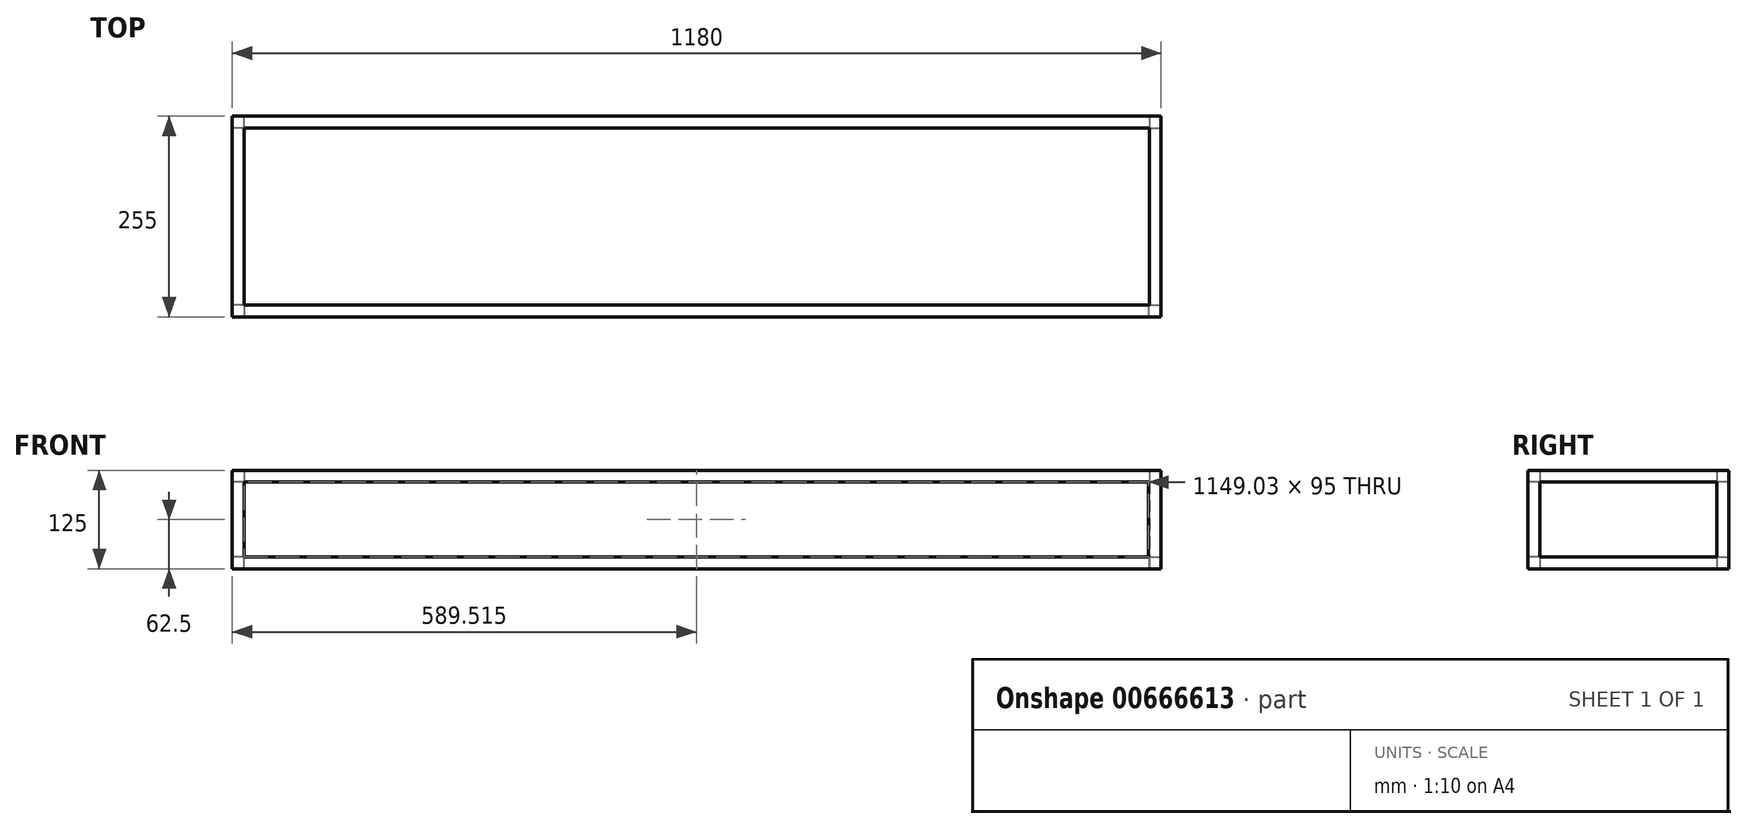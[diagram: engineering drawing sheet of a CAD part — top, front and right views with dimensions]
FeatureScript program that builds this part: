
annotation { "Feature Type Name" : "Feature", "Feature Type Description" : "" }
export const myFeature = defineFeature(function(context is Context, id is Id, definition is map)
    precondition{}
    {
        {
            var Q0;
            Q0=qCreatedBy(makeId("Top.planeOp"),FACE);
            var sketch = newSketch(context, id + "F0", { "sketchPlane" : qUnion([Q0])});
            skLineSegment(sketch, "E0.bottom", {"start": v(0, 0) * mm, "end": v(-1180, 0) * mm});
            skLineSegment(sketch, "E0.top", {"start": v(0, 255) * mm, "end": v(-1180, 255) * mm});
            skLineSegment(sketch, "E0.left", {"start": v(0, 0) * mm, "end": v(0, 255) * mm});
            skLineSegment(sketch, "E0.right", {"start": v(-1180, 0) * mm, "end": v(-1180, 255) * mm});
            skLineSegment(sketch, "E1.0", {"start": v(-15, 240) * mm, "end": v(-1165, 240) * mm});
            skLineSegment(sketch, "E1.1", {"start": v(-15, 15) * mm, "end": v(-15, 240) * mm});
            skLineSegment(sketch, "E1.2", {"start": v(-15, 15) * mm, "end": v(-1165, 15) * mm});
            skLineSegment(sketch, "E1.3", {"start": v(-1165, 15) * mm, "end": v(-1165, 240) * mm});
            skSolve(sketch);
        }
        {
            var Q0;
            Q0 = qSketchRegion(id + "F0", true);
            extrude(context, id + "F1", {"entities" : qUnion([Q0]), "depth" : 15 * mm, "offsetDistance" : 25 * mm});
        }
        {
            var Q0;
            Q0=qCreatedBy(makeId("Front.planeOp"),FACE);
            var sketch = newSketch(context, id + "F2", { "sketchPlane" : qUnion([Q0])});
            skLineSegment(sketch, "E2.bottom", {"start": v(0, 0) * mm, "end": v(-15.97, 0) * mm});
            skLineSegment(sketch, "E2.top", {"start": v(0, -110) * mm, "end": v(-1180, -110) * mm});
            skLineSegment(sketch, "E2.left", {"start": v(0, 0) * mm, "end": v(0, -110) * mm});
            skLineSegment(sketch, "E2.right", {"start": v(-1180, 0) * mm, "end": v(-1180, -110) * mm});
            skLineSegment(sketch, "E3.1", {"start": v(-15.97, -15) * mm, "end": v(-15.97, -95) * mm});
            skLineSegment(sketch, "E3.2", {"start": v(-15.97, -95) * mm, "end": v(-1165, -95) * mm});
            skLineSegment(sketch, "E3.3", {"start": v(-1165, -15) * mm, "end": v(-1165, -95) * mm});
            skLineSegment(sketch, "E4", {"start": v(-1165, -15) * mm, "end": v(-1165, 0) * mm});
            skLineSegment(sketch, "E5", {"start": v(-15.97, -15) * mm, "end": v(-15.97, 0) * mm});
            skLineSegment(sketch, "E6.trimOffspring", {"start": v(-1165, 0) * mm, "end": v(-1180, 0) * mm});
            skSolve(sketch);
        }
        {
            var Q0;
            Q0 = qSketchRegion(id + "F2", true);
            extrude(context, id + "F3", {"entities" : qUnion([Q0]), "operationType" : NewBodyOperationType.ADD, "oppositeDirection" : true, "depth" : 15 * mm, "offsetDistance" : 25 * mm});
        }
        {
            var Q0;
            Q0=qCreatedBy(makeId("Right.planeOp"),FACE);
            var sketch = newSketch(context, id + "F4", { "sketchPlane" : qUnion([Q0])});
            skLineSegment(sketch, "E7", {"start": v(0, 0) * mm, "end": v(0, -110) * mm, "construction": true});
            skLineSegment(sketch, "E8", {"start": v(0, -110) * mm, "end": v(15, -110) * mm, "construction": true});
            skLineSegment(sketch, "E9", {"start": v(15, -110) * mm, "end": v(255, -110) * mm});
            skLineSegment(sketch, "E10", {"start": v(255, -110) * mm, "end": v(255, 0) * mm});
            skLineSegment(sketch, "E11", {"start": v(255, 0) * mm, "end": v(240, 0) * mm});
            skLineSegment(sketch, "E12", {"start": v(240, 0) * mm, "end": v(240, -95) * mm});
            skLineSegment(sketch, "E13", {"start": v(240, -95) * mm, "end": v(15, -95) * mm});
            skLineSegment(sketch, "E14", {"start": v(15, -95) * mm, "end": v(15, -110) * mm});
            skSolve(sketch);
        }
        {
            var Q0;
            Q0 = qSketchRegion(id + "F4", true);
            extrude(context, id + "F5", {"entities" : qUnion([Q0]), "operationType" : NewBodyOperationType.ADD, "oppositeDirection" : true, "depth" : 15 * mm, "offsetDistance" : 25 * mm});
        }
        {
            var Q0;
            Q0=makeQuery(id+"F3.boolean.opBoolean","MERGE",FACE,{"derivedFrom":[makeQuery(id+"F1.opExtrude","SWEPT_FACE",FACE,{"disambiguationData":[OSD([sQuery(id+"F0.wireOp",EDGE,"E0.right")])]}),makeQuery(id+"F3.opExtrude","SWEPT_FACE",FACE,{"disambiguationData":[OSD([sQuery(id+"F2.wireOp",EDGE,"E2.right")])]})]});
            cPlane(context, id + "F6", {"entities" : qUnion([Q0]), "cplaneType" : CPlaneType.OFFSET, "offset" : 0 * mm, "width" : 150 * mm, "height" : 150 * mm});
        }
        {
            var Q0;
            Q0=qCreatedBy(id+"F6.planeOp",FACE);
            var sketch = newSketch(context, id + "F7", { "sketchPlane" : qUnion([Q0])});
            skLineSegment(sketch, "E15", {"start": v(0, 0) * mm, "end": v(0, -110) * mm, "construction": true});
            skLineSegment(sketch, "E16", {"start": v(0, -110) * mm, "end": v(-15, -110) * mm, "construction": true});
            skLineSegment(sketch, "E17", {"start": v(-15, -110) * mm, "end": v(-255, -110) * mm});
            skLineSegment(sketch, "E18", {"start": v(-255, -110) * mm, "end": v(-255, 0) * mm});
            skLineSegment(sketch, "E19", {"start": v(-255, 0) * mm, "end": v(-240, 0) * mm});
            skLineSegment(sketch, "E20", {"start": v(-240, 0) * mm, "end": v(-240, -95) * mm});
            skLineSegment(sketch, "E21", {"start": v(-240, -95) * mm, "end": v(-15, -95) * mm});
            skLineSegment(sketch, "E22", {"start": v(-15, -95) * mm, "end": v(-15, -110) * mm});
            skSolve(sketch);
        }
        {
            var Q0;
            Q0 = qSketchRegion(id + "F7", true);
            extrude(context, id + "F8", {"entities" : qUnion([Q0]), "oppositeDirection" : true, "depth" : 15 * mm, "offsetDistance" : 25 * mm});
        }
        {
            var Q0;
            Q0=makeQuery(id+"F5.boolean.opBoolean","MERGE",FACE,{"derivedFrom":[makeQuery(id+"F1.opExtrude","SWEPT_FACE",FACE,{"disambiguationData":[OSD([sQuery(id+"F0.wireOp",EDGE,"E0.top")])]}),makeQuery(id+"F5.opExtrude","SWEPT_FACE",FACE,{"disambiguationData":[OSD([sQuery(id+"F4.wireOp",EDGE,"E10")])]})]});
            cPlane(context, id + "F9", {"entities" : qUnion([Q0]), "cplaneType" : CPlaneType.OFFSET, "offset" : 0 * mm, "width" : 150 * mm, "height" : 150 * mm});
        }
        {
            var Q0;
            Q0=qCreatedBy(id+"F9.planeOp",FACE);
            var sketch = newSketch(context, id + "F10", { "sketchPlane" : qUnion([Q0])});
            skLineSegment(sketch, "E23", {"start": v(0, 0) * mm, "end": v(0, -110) * mm, "construction": true});
            skLineSegment(sketch, "E24", {"start": v(0, -110) * mm, "end": v(15, -110) * mm, "construction": true});
            skLineSegment(sketch, "E25", {"start": v(15, -110) * mm, "end": v(1165, -110) * mm});
            skLineSegment(sketch, "E26", {"start": v(1165, -110) * mm, "end": v(1165, -95) * mm});
            skLineSegment(sketch, "E27", {"start": v(1165, -95) * mm, "end": v(15, -95) * mm});
            skLineSegment(sketch, "E28", {"start": v(15, -95) * mm, "end": v(15, -110) * mm});
            skSolve(sketch);
        }
        {
            var Q0;
            Q0 = qSketchRegion(id + "F10", true);
            extrude(context, id + "F11", {"entities" : qUnion([Q0]), "oppositeDirection" : true, "depth" : 15 * mm, "offsetDistance" : 25 * mm});
        }
    });
